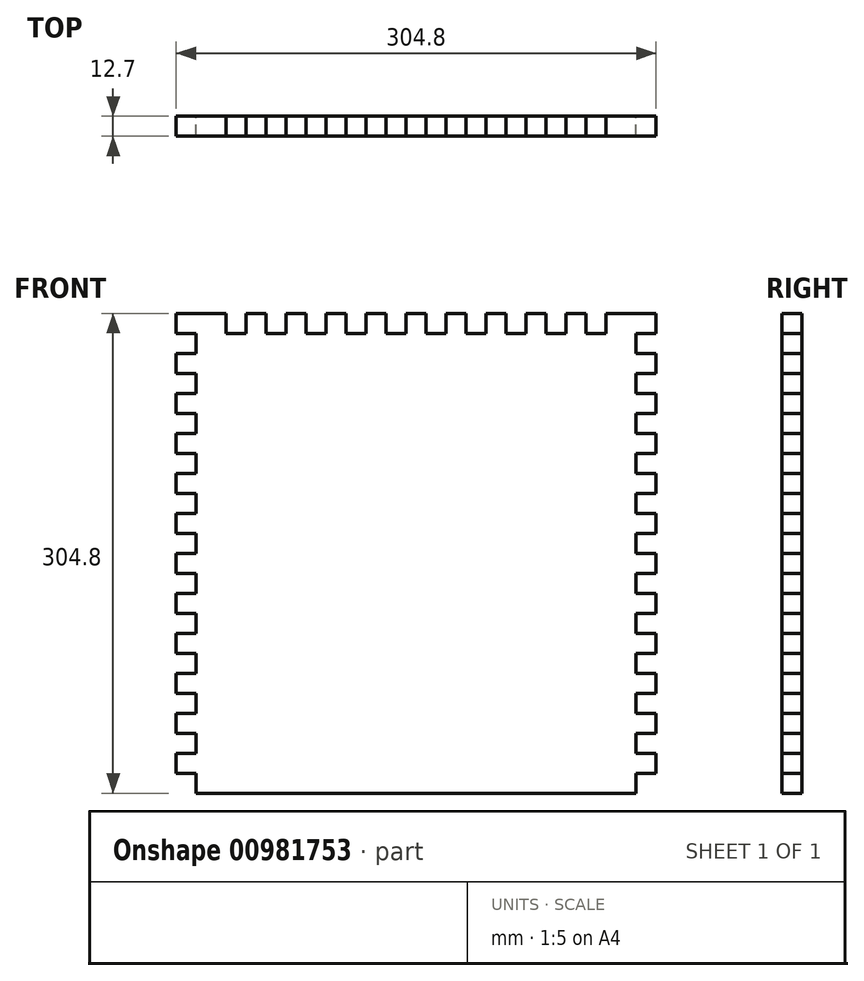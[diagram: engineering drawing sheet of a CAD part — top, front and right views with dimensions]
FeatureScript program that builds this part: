
annotation { "Feature Type Name" : "Feature", "Feature Type Description" : "" }
export const myFeature = defineFeature(function(context is Context, id is Id, definition is map)
    precondition{}
    {
        {
            var Q0;
            Q0=qCreatedBy(makeId("Front.planeOp"),FACE);
            var sketch = newSketch(context, id + "F0", { "sketchPlane" : qUnion([Q0])});
            skPoint(sketch, "E0.middle", {"position": v(0, 0) * mm});
            skLineSegment(sketch, "E1", {"start": v(152.4, 152.4) * mm, "end": v(152.4, 139.7) * mm});
            skLineSegment(sketch, "E2", {"start": v(152.4, 139.7) * mm, "end": v(139.7, 139.7) * mm});
            skLineSegment(sketch, "E3", {"start": v(139.7, 139.7) * mm, "end": v(139.7, 127) * mm});
            skLineSegment(sketch, "E4", {"start": v(139.7, 127) * mm, "end": v(152.4, 127) * mm});
            skLineSegment(sketch, "E5.0.1.0", {"start": v(152.4, 114.3) * mm, "end": v(139.7, 114.3) * mm});
            skLineSegment(sketch, "E5.0.1.1", {"start": v(139.7, 101.6) * mm, "end": v(152.4, 101.6) * mm});
            skLineSegment(sketch, "E5.0.1.2", {"start": v(139.7, 114.3) * mm, "end": v(139.7, 101.6) * mm});
            skLineSegment(sketch, "E5.0.1.3", {"start": v(152.4, 127) * mm, "end": v(152.4, 114.3) * mm});
            skLineSegment(sketch, "E5.0.2.0", {"start": v(152.4, 88.9) * mm, "end": v(139.7, 88.9) * mm});
            skLineSegment(sketch, "E5.0.2.1", {"start": v(139.7, 76.2) * mm, "end": v(152.4, 76.2) * mm});
            skLineSegment(sketch, "E5.0.2.2", {"start": v(139.7, 88.9) * mm, "end": v(139.7, 76.2) * mm});
            skLineSegment(sketch, "E5.0.2.3", {"start": v(152.4, 101.6) * mm, "end": v(152.4, 88.9) * mm});
            skLineSegment(sketch, "E5.0.3.0", {"start": v(152.4, 63.5) * mm, "end": v(139.7, 63.5) * mm});
            skLineSegment(sketch, "E5.0.3.1", {"start": v(139.7, 50.8) * mm, "end": v(152.4, 50.8) * mm});
            skLineSegment(sketch, "E5.0.3.2", {"start": v(139.7, 63.5) * mm, "end": v(139.7, 50.8) * mm});
            skLineSegment(sketch, "E5.0.3.3", {"start": v(152.4, 76.2) * mm, "end": v(152.4, 63.5) * mm});
            skLineSegment(sketch, "E5.0.4.0", {"start": v(152.4, 38.1) * mm, "end": v(139.7, 38.1) * mm});
            skLineSegment(sketch, "E5.0.4.1", {"start": v(139.7, 25.4) * mm, "end": v(152.4, 25.4) * mm});
            skLineSegment(sketch, "E5.0.4.2", {"start": v(139.7, 38.1) * mm, "end": v(139.7, 25.4) * mm});
            skLineSegment(sketch, "E5.0.4.3", {"start": v(152.4, 50.8) * mm, "end": v(152.4, 38.1) * mm});
            skLineSegment(sketch, "E5.0.5.0", {"start": v(152.4, 12.7) * mm, "end": v(139.7, 12.7) * mm});
            skLineSegment(sketch, "E5.0.5.1", {"start": v(139.7, 0) * mm, "end": v(152.4, 0) * mm});
            skLineSegment(sketch, "E5.0.5.2", {"start": v(139.7, 12.7) * mm, "end": v(139.7, 0) * mm});
            skLineSegment(sketch, "E5.0.5.3", {"start": v(152.4, 25.4) * mm, "end": v(152.4, 12.7) * mm});
            skLineSegment(sketch, "E5.0.6.0", {"start": v(152.4, -12.7) * mm, "end": v(139.7, -12.7) * mm});
            skLineSegment(sketch, "E5.0.6.1", {"start": v(139.7, -25.4) * mm, "end": v(152.4, -25.4) * mm});
            skLineSegment(sketch, "E5.0.6.2", {"start": v(139.7, -12.7) * mm, "end": v(139.7, -25.4) * mm});
            skLineSegment(sketch, "E5.0.6.3", {"start": v(152.4, 0) * mm, "end": v(152.4, -12.7) * mm});
            skLineSegment(sketch, "E5.0.7.0", {"start": v(152.4, -38.1) * mm, "end": v(139.7, -38.1) * mm});
            skLineSegment(sketch, "E5.0.7.1", {"start": v(139.7, -50.8) * mm, "end": v(152.4, -50.8) * mm});
            skLineSegment(sketch, "E5.0.7.2", {"start": v(139.7, -38.1) * mm, "end": v(139.7, -50.8) * mm});
            skLineSegment(sketch, "E5.0.7.3", {"start": v(152.4, -25.4) * mm, "end": v(152.4, -38.1) * mm});
            skLineSegment(sketch, "E5.0.8.0", {"start": v(152.4, -63.5) * mm, "end": v(139.7, -63.5) * mm});
            skLineSegment(sketch, "E5.0.8.1", {"start": v(139.7, -76.2) * mm, "end": v(152.4, -76.2) * mm});
            skLineSegment(sketch, "E5.0.8.2", {"start": v(139.7, -63.5) * mm, "end": v(139.7, -76.2) * mm});
            skLineSegment(sketch, "E5.0.8.3", {"start": v(152.4, -50.8) * mm, "end": v(152.4, -63.5) * mm});
            skLineSegment(sketch, "E5.0.9.0", {"start": v(152.4, -88.9) * mm, "end": v(139.7, -88.9) * mm});
            skLineSegment(sketch, "E5.0.9.1", {"start": v(139.7, -101.6) * mm, "end": v(152.4, -101.6) * mm});
            skLineSegment(sketch, "E5.0.9.2", {"start": v(139.7, -88.9) * mm, "end": v(139.7, -101.6) * mm});
            skLineSegment(sketch, "E5.0.9.3", {"start": v(152.4, -76.2) * mm, "end": v(152.4, -88.9) * mm});
            skLineSegment(sketch, "E5.0.10.0", {"start": v(152.4, -114.3) * mm, "end": v(139.7, -114.3) * mm});
            skLineSegment(sketch, "E5.0.10.1", {"start": v(139.7, -127) * mm, "end": v(152.4, -127) * mm});
            skLineSegment(sketch, "E5.0.10.2", {"start": v(139.7, -114.3) * mm, "end": v(139.7, -127) * mm});
            skLineSegment(sketch, "E5.0.10.3", {"start": v(152.4, -101.6) * mm, "end": v(152.4, -114.3) * mm});
            skLineSegment(sketch, "E5.0.11.0", {"start": v(152.4, -139.7) * mm, "end": v(139.7, -139.7) * mm});
            skLineSegment(sketch, "E5.0.11.2", {"start": v(139.7, -139.7) * mm, "end": v(139.7, -152.4) * mm});
            skLineSegment(sketch, "E5.0.11.3", {"start": v(152.4, -127) * mm, "end": v(152.4, -139.7) * mm});
            skLineSegment(sketch, "E5.direction1", {"start": v(139.7, 127) * mm, "end": v(165.1, 127) * mm, "construction": true});
            skLineSegment(sketch, "E5.direction2", {"start": v(139.7, 127) * mm, "end": v(139.7, 101.6) * mm, "construction": true});
            skLineSegment(sketch, "E6", {"start": v(-152.4, 152.4) * mm, "end": v(-152.4, 139.7) * mm});
            skLineSegment(sketch, "E7", {"start": v(-152.4, 139.7) * mm, "end": v(-139.7, 139.7) * mm});
            skLineSegment(sketch, "E8", {"start": v(-139.7, 139.7) * mm, "end": v(-139.7, 127) * mm});
            skLineSegment(sketch, "E9", {"start": v(-139.7, 127) * mm, "end": v(-152.4, 127) * mm});
            skLineSegment(sketch, "E10.0.1.0", {"start": v(-152.4, 127) * mm, "end": v(-152.4, 114.3) * mm});
            skLineSegment(sketch, "E10.0.1.1", {"start": v(-139.7, 114.3) * mm, "end": v(-139.7, 101.6) * mm});
            skLineSegment(sketch, "E10.0.1.2", {"start": v(-139.7, 101.6) * mm, "end": v(-152.4, 101.6) * mm});
            skLineSegment(sketch, "E10.0.1.3", {"start": v(-152.4, 114.3) * mm, "end": v(-139.7, 114.3) * mm});
            skLineSegment(sketch, "E10.0.2.0", {"start": v(-152.4, 101.6) * mm, "end": v(-152.4, 88.9) * mm});
            skLineSegment(sketch, "E10.0.2.1", {"start": v(-139.7, 88.9) * mm, "end": v(-139.7, 76.2) * mm});
            skLineSegment(sketch, "E10.0.2.2", {"start": v(-139.7, 76.2) * mm, "end": v(-152.4, 76.2) * mm});
            skLineSegment(sketch, "E10.0.2.3", {"start": v(-152.4, 88.9) * mm, "end": v(-139.7, 88.9) * mm});
            skLineSegment(sketch, "E10.0.3.0", {"start": v(-152.4, 76.2) * mm, "end": v(-152.4, 63.5) * mm});
            skLineSegment(sketch, "E10.0.3.1", {"start": v(-139.7, 63.5) * mm, "end": v(-139.7, 50.8) * mm});
            skLineSegment(sketch, "E10.0.3.2", {"start": v(-139.7, 50.8) * mm, "end": v(-152.4, 50.8) * mm});
            skLineSegment(sketch, "E10.0.3.3", {"start": v(-152.4, 63.5) * mm, "end": v(-139.7, 63.5) * mm});
            skLineSegment(sketch, "E10.0.4.0", {"start": v(-152.4, 50.8) * mm, "end": v(-152.4, 38.1) * mm});
            skLineSegment(sketch, "E10.0.4.1", {"start": v(-139.7, 38.1) * mm, "end": v(-139.7, 25.4) * mm});
            skLineSegment(sketch, "E10.0.4.2", {"start": v(-139.7, 25.4) * mm, "end": v(-152.4, 25.4) * mm});
            skLineSegment(sketch, "E10.0.4.3", {"start": v(-152.4, 38.1) * mm, "end": v(-139.7, 38.1) * mm});
            skLineSegment(sketch, "E10.0.5.0", {"start": v(-152.4, 25.4) * mm, "end": v(-152.4, 12.7) * mm});
            skLineSegment(sketch, "E10.0.5.1", {"start": v(-139.7, 12.7) * mm, "end": v(-139.7, 0) * mm});
            skLineSegment(sketch, "E10.0.5.2", {"start": v(-139.7, 0) * mm, "end": v(-152.4, 0) * mm});
            skLineSegment(sketch, "E10.0.5.3", {"start": v(-152.4, 12.7) * mm, "end": v(-139.7, 12.7) * mm});
            skLineSegment(sketch, "E10.0.6.0", {"start": v(-152.4, 0) * mm, "end": v(-152.4, -12.7) * mm});
            skLineSegment(sketch, "E10.0.6.1", {"start": v(-139.7, -12.7) * mm, "end": v(-139.7, -25.4) * mm});
            skLineSegment(sketch, "E10.0.6.2", {"start": v(-139.7, -25.4) * mm, "end": v(-152.4, -25.4) * mm});
            skLineSegment(sketch, "E10.0.6.3", {"start": v(-152.4, -12.7) * mm, "end": v(-139.7, -12.7) * mm});
            skLineSegment(sketch, "E10.0.7.0", {"start": v(-152.4, -25.4) * mm, "end": v(-152.4, -38.1) * mm});
            skLineSegment(sketch, "E10.0.7.1", {"start": v(-139.7, -38.1) * mm, "end": v(-139.7, -50.8) * mm});
            skLineSegment(sketch, "E10.0.7.2", {"start": v(-139.7, -50.8) * mm, "end": v(-152.4, -50.8) * mm});
            skLineSegment(sketch, "E10.0.7.3", {"start": v(-152.4, -38.1) * mm, "end": v(-139.7, -38.1) * mm});
            skLineSegment(sketch, "E10.0.8.0", {"start": v(-152.4, -50.8) * mm, "end": v(-152.4, -63.5) * mm});
            skLineSegment(sketch, "E10.0.8.1", {"start": v(-139.7, -63.5) * mm, "end": v(-139.7, -76.2) * mm});
            skLineSegment(sketch, "E10.0.8.2", {"start": v(-139.7, -76.2) * mm, "end": v(-152.4, -76.2) * mm});
            skLineSegment(sketch, "E10.0.8.3", {"start": v(-152.4, -63.5) * mm, "end": v(-139.7, -63.5) * mm});
            skLineSegment(sketch, "E10.0.9.0", {"start": v(-152.4, -76.2) * mm, "end": v(-152.4, -88.9) * mm});
            skLineSegment(sketch, "E10.0.9.1", {"start": v(-139.7, -88.9) * mm, "end": v(-139.7, -101.6) * mm});
            skLineSegment(sketch, "E10.0.9.2", {"start": v(-139.7, -101.6) * mm, "end": v(-152.4, -101.6) * mm});
            skLineSegment(sketch, "E10.0.9.3", {"start": v(-152.4, -88.9) * mm, "end": v(-139.7, -88.9) * mm});
            skLineSegment(sketch, "E10.0.10.0", {"start": v(-152.4, -101.6) * mm, "end": v(-152.4, -114.3) * mm});
            skLineSegment(sketch, "E10.0.10.1", {"start": v(-139.7, -114.3) * mm, "end": v(-139.7, -127) * mm});
            skLineSegment(sketch, "E10.0.10.2", {"start": v(-139.7, -127) * mm, "end": v(-152.4, -127) * mm});
            skLineSegment(sketch, "E10.0.10.3", {"start": v(-152.4, -114.3) * mm, "end": v(-139.7, -114.3) * mm});
            skLineSegment(sketch, "E10.0.11.0", {"start": v(-152.4, -127) * mm, "end": v(-152.4, -139.7) * mm});
            skLineSegment(sketch, "E10.0.11.1", {"start": v(-139.7, -139.7) * mm, "end": v(-139.7, -152.4) * mm});
            skLineSegment(sketch, "E10.0.11.3", {"start": v(-152.4, -139.7) * mm, "end": v(-139.7, -139.7) * mm});
            skLineSegment(sketch, "E10.direction1", {"start": v(-152.4, 127) * mm, "end": v(-127, 127) * mm, "construction": true});
            skLineSegment(sketch, "E10.direction2", {"start": v(-152.4, 127) * mm, "end": v(-152.4, 101.6) * mm, "construction": true});
            skLineSegment(sketch, "E11", {"start": v(-139.7, -152.4) * mm, "end": v(139.7, -152.4) * mm});
            skLineSegment(sketch, "E12", {"start": v(-120.65, 152.4) * mm, "end": v(-120.65, 139.7) * mm});
            skLineSegment(sketch, "E13", {"start": v(-120.65, 139.7) * mm, "end": v(-107.95, 139.7) * mm});
            skLineSegment(sketch, "E14", {"start": v(-107.95, 139.7) * mm, "end": v(-107.95, 152.4) * mm});
            skLineSegment(sketch, "E15", {"start": v(-107.95, 152.4) * mm, "end": v(-95.25, 152.4) * mm});
            skLineSegment(sketch, "E16", {"start": v(-152.4, 152.4) * mm, "end": v(-120.65, 152.4) * mm});
            skLineSegment(sketch, "E17.1.0.0", {"start": v(-82.55, 139.7) * mm, "end": v(-82.55, 152.4) * mm});
            skLineSegment(sketch, "E17.1.0.1", {"start": v(-95.25, 152.4) * mm, "end": v(-95.25, 139.7) * mm});
            skLineSegment(sketch, "E17.1.0.2", {"start": v(-95.25, 139.7) * mm, "end": v(-82.55, 139.7) * mm});
            skLineSegment(sketch, "E17.1.0.3", {"start": v(-82.55, 152.4) * mm, "end": v(-69.85, 152.4) * mm});
            skLineSegment(sketch, "E17.2.0.0", {"start": v(-57.15, 139.7) * mm, "end": v(-57.15, 152.4) * mm});
            skLineSegment(sketch, "E17.2.0.1", {"start": v(-69.85, 152.4) * mm, "end": v(-69.85, 139.7) * mm});
            skLineSegment(sketch, "E17.2.0.2", {"start": v(-69.85, 139.7) * mm, "end": v(-57.15, 139.7) * mm});
            skLineSegment(sketch, "E17.2.0.3", {"start": v(-57.15, 152.4) * mm, "end": v(-44.45, 152.4) * mm});
            skLineSegment(sketch, "E17.3.0.0", {"start": v(-31.75, 139.7) * mm, "end": v(-31.75, 152.4) * mm});
            skLineSegment(sketch, "E17.3.0.1", {"start": v(-44.45, 152.4) * mm, "end": v(-44.45, 139.7) * mm});
            skLineSegment(sketch, "E17.3.0.2", {"start": v(-44.45, 139.7) * mm, "end": v(-31.75, 139.7) * mm});
            skLineSegment(sketch, "E17.3.0.3", {"start": v(-31.75, 152.4) * mm, "end": v(-19.05, 152.4) * mm});
            skLineSegment(sketch, "E17.4.0.0", {"start": v(-6.35, 139.7) * mm, "end": v(-6.35, 152.4) * mm});
            skLineSegment(sketch, "E17.4.0.1", {"start": v(-19.05, 152.4) * mm, "end": v(-19.05, 139.7) * mm});
            skLineSegment(sketch, "E17.4.0.2", {"start": v(-19.05, 139.7) * mm, "end": v(-6.35, 139.7) * mm});
            skLineSegment(sketch, "E17.4.0.3", {"start": v(-6.35, 152.4) * mm, "end": v(6.35, 152.4) * mm});
            skLineSegment(sketch, "E17.5.0.0", {"start": v(19.05, 139.7) * mm, "end": v(19.05, 152.4) * mm});
            skLineSegment(sketch, "E17.5.0.1", {"start": v(6.35, 152.4) * mm, "end": v(6.35, 139.7) * mm});
            skLineSegment(sketch, "E17.5.0.2", {"start": v(6.35, 139.7) * mm, "end": v(19.05, 139.7) * mm});
            skLineSegment(sketch, "E17.5.0.3", {"start": v(19.05, 152.4) * mm, "end": v(31.75, 152.4) * mm});
            skLineSegment(sketch, "E17.6.0.0", {"start": v(44.45, 139.7) * mm, "end": v(44.45, 152.4) * mm});
            skLineSegment(sketch, "E17.6.0.1", {"start": v(31.75, 152.4) * mm, "end": v(31.75, 139.7) * mm});
            skLineSegment(sketch, "E17.6.0.2", {"start": v(31.75, 139.7) * mm, "end": v(44.45, 139.7) * mm});
            skLineSegment(sketch, "E17.6.0.3", {"start": v(44.45, 152.4) * mm, "end": v(57.15, 152.4) * mm});
            skLineSegment(sketch, "E17.7.0.0", {"start": v(69.85, 139.7) * mm, "end": v(69.85, 152.4) * mm});
            skLineSegment(sketch, "E17.7.0.1", {"start": v(57.15, 152.4) * mm, "end": v(57.15, 139.7) * mm});
            skLineSegment(sketch, "E17.7.0.2", {"start": v(57.15, 139.7) * mm, "end": v(69.85, 139.7) * mm});
            skLineSegment(sketch, "E17.7.0.3", {"start": v(69.85, 152.4) * mm, "end": v(82.55, 152.4) * mm});
            skLineSegment(sketch, "E17.8.0.0", {"start": v(95.25, 139.7) * mm, "end": v(95.25, 152.4) * mm});
            skLineSegment(sketch, "E17.8.0.1", {"start": v(82.55, 152.4) * mm, "end": v(82.55, 139.7) * mm});
            skLineSegment(sketch, "E17.8.0.2", {"start": v(82.55, 139.7) * mm, "end": v(95.25, 139.7) * mm});
            skLineSegment(sketch, "E17.8.0.3", {"start": v(95.25, 152.4) * mm, "end": v(107.95, 152.4) * mm});
            skLineSegment(sketch, "E17.9.0.0", {"start": v(120.65, 139.7) * mm, "end": v(120.65, 152.4) * mm});
            skLineSegment(sketch, "E17.9.0.1", {"start": v(107.95, 152.4) * mm, "end": v(107.95, 139.7) * mm});
            skLineSegment(sketch, "E17.9.0.2", {"start": v(107.95, 139.7) * mm, "end": v(120.65, 139.7) * mm});
            skLineSegment(sketch, "E17.direction1", {"start": v(-120.65, 139.7) * mm, "end": v(-95.25, 139.7) * mm, "construction": true});
            skLineSegment(sketch, "E18", {"start": v(120.65, 152.4) * mm, "end": v(152.4, 152.4) * mm});
            skLineSegment(sketch, "E19", {"start": v(139.7, 139.7) * mm, "end": v(139.7, 152.4) * mm});
            skLineSegment(sketch, "E20", {"start": v(-139.7, 139.7) * mm, "end": v(-139.7, 152.4) * mm});
            skSolve(sketch);
        }
        {
            var Q0;
            Q0 = qSketchRegion(id + "F0", true);
            extrude(context, id + "F1", {"entities" : qUnion([Q0]), "depth" : 12.7 * mm, "offsetDistance" : 25.4 * mm});
        }
    });
